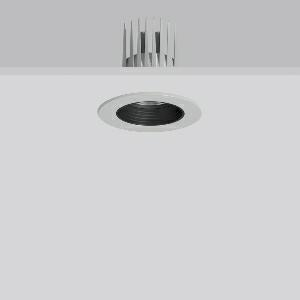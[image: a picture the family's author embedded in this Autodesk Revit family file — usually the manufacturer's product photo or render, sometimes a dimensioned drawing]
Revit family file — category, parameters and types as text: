
# Revit family: heledon_mini_e_901753_004_2_4503
name_source: partatom
category: Lighting Fixtures
units: mm (PartAtom-declared; Revit-internal decimal feet)

## family parameters
Cut with Voids When Loaded = No
Host = Face
Light Source = No
Part Type = Normal
Room Calculation Point = No
Round Connector Dimension = Use Diameter
Shared = No

## types (1)
- HELEDON mini E (1 x LED Modul 927, 2700 lm, 2700)
    Apparent Load = 29 VA
    Approval mark = CE
    CIE Flux Codes = 98 100 100 100 100
    Color Rendering = 92
    Color Temperature = 2700
    Default Elevation = 1800 mm
    Description = Series: HELEDON mini
Round recessed downlight. Housing: die-cast aluminium, powder-coated. Black plastic ring and recessed LED to prevent glare from the side. Optical assembly with lens made of plastic (polycarbonate) for the best homogeneous light distribution - can be changed without tools. Best colour rendering index Ra>90. Suitable for Recessed ceiling mounting. Installation without tools thanks to spring fastening system. Including separate LED converter with connecting cable 600 mm.High quality converter without flickering and stroboscopic effect. Through-wiring box (5 pole) available as accessory. The following accessories can be mounted without use of tools: interchangeable lenses, decorative glasses, honeycomb louvre, clear and frosted diffusers, white interchangeable plastic ring. 
Colour: silver
Diameter: 124 mm
Height: 3 mm
Cut-out diameter: 114 mm
Recess height: 170 mm
Luminaire: recess height: 120 mm
Lamp: LED
Socket: without socket
Colour temperature: 2700K
Colour rendering index (CRI): 92
System power: 29 W
Rated luminous flux: 2700 lm
Luminous efficiency: 93 lm/W
Control gear: Regulated power supply
Protection class: II
Type of protection: IP 20
    Height = 0 mm  [stored 0 ft]
    Lamp = 1 x LED Modul 927
    Lamp Light Flux = 2700 lm
    Lamp count = 1
    Length = 124 mm  [stored 0.406824 ft]
    Lifetime = 50000 h
    Luminous efficacy = 93 lm/W
    Manufacturer = RZB
    ModVariant = No
    Model = 901753.004.2
    Mounting Place = Ceiling
    Mounting Type = Recessed
    Number of Poles = 1
    OnlyDefault = Yes
    Power Factor = 1
    Product Name = HELEDON mini E
    Product group = Recessed downlights
    ProductGroupID = 402
    Protection Class = Protection class II
    Protection Degree = IP 20
    RLX_Detail_Level = 1
    RLX_Emergency_Light_Flux = 0 lm
    RLX_Emergency_Type = 0
    RLX_Emergency_Type_DB = No
    RlxData = <blob elided: 127321 chars, md5=25b60eab>
    Socket = socket
    Standby Power = 0 W
    System Light Flux = 2700 lm
    System Power = 29 W
    Type Comments = Product without accessories
    Type Image = 901656.004.jpg
    URL = http://relux.com
    VarID = ---
    Voltage = 230 V
    Voltage Range = 220-240 V
    Weight = 0.00 kg
    Width = 0 mm  [stored 0 ft]

note: [stored X ft] marks values corroborated as IEEE doubles in the binary element streams (Revit-internal decimal feet)

## geometry (parser evidence)
native form markers: Blend x4, Sweep x12
no freeform markers — native parametric forms only
